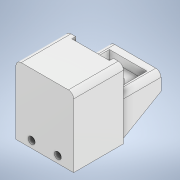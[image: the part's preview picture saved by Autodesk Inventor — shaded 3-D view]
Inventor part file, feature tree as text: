
AUTODESK INVENTOR PART (.ipt)
format: ipt  version: 2020 (Build 240168000, 168)  size: 320,000 bytes
history: native  units: mm
features: extrude x10, sketch x6, other x2, mirror x1, fillet x1, projected_geometry x1
ambient origin geometry x8: Origin, YZ Plane, XZ Plane, XY Plane, X Axis, Y Axis, Z Axis, Center Point
bodies: Body1 (feature_tree)
feature tree (21):
  extrude  "Wyciągnięcie proste8"  Depth=20.5mm
  sketch  "Szkic8"
  other  "Płaszczyzna konstrukcyjna1"
  extrude  "Wyciągnięcie proste9"  Depth=20.5mm
  extrude  "Wyciągnięcie proste14"  Depth=20.5mm
  mirror  "Odbij1"
  extrude  "Wyciągnięcie proste10"  Depth=20.5mm
  extrude  "Wyciągnięcie proste11"  Depth=50.0mm
  extrude  "Wyciągnięcie proste12"  Depth=25.0mm
  extrude  "Wyciągnięcie proste13"  Depth=8.0mm
  sketch  "Szkic12"
  extrude  "Wyciągnięcie proste17"  Depth=8.0mm
  extrude  "Wyciągnięcie proste15"  Depth=8.0mm
  extrude  "Wyciągnięcie proste16"  Depth=75.0mm TaperAngle=0.0deg
  fillet  "Zaokrąglenie1"  Radius=22.0mm
  other  "Pogrubienie1"
  sketch  "Szkic7"
  sketch  "Szkic9"
  sketch  "Szkic10"
  sketch  "Szkic13"
  projected_geometry  "Pętla rzutowana1"
